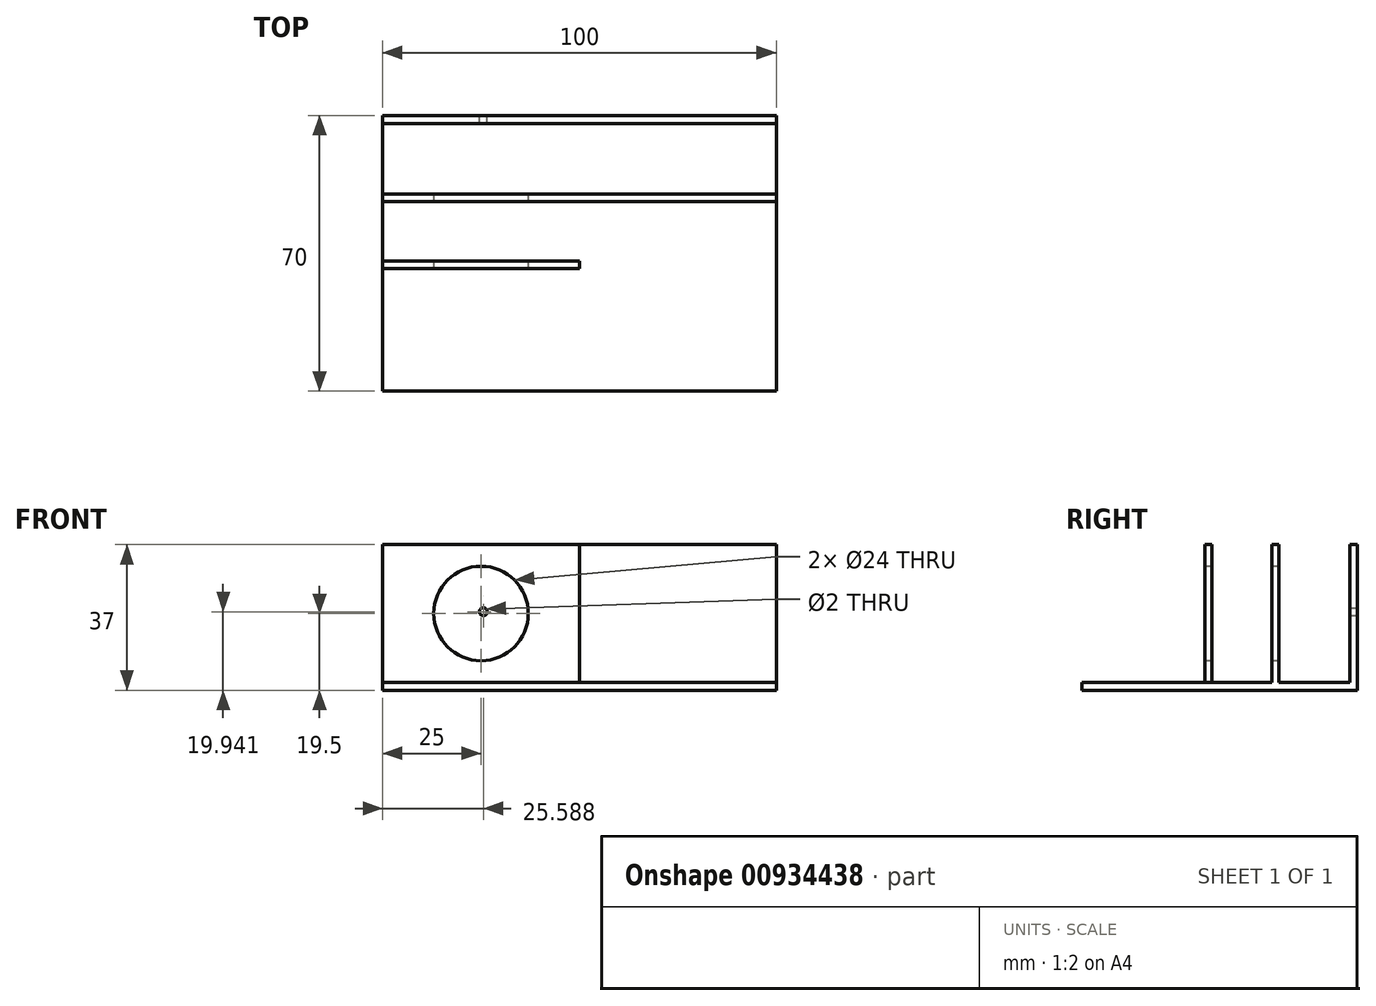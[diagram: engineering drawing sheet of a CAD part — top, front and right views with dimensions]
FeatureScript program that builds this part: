
annotation { "Feature Type Name" : "Feature", "Feature Type Description" : "" }
export const myFeature = defineFeature(function(context is Context, id is Id, definition is map)
    precondition{}
    {
        {
            var Q0;
            Q0=qCreatedBy(makeId("Top.planeOp"),FACE);
            var sketch = newSketch(context, id + "F0", { "sketchPlane" : qUnion([Q0])});
            skLineSegment(sketch, "E0.bottom", {"start": v(-50, 35) * mm, "end": v(50, 35) * mm});
            skLineSegment(sketch, "E0.top", {"start": v(-50, -35) * mm, "end": v(50, -35) * mm});
            skLineSegment(sketch, "E0.left", {"start": v(-50, 35) * mm, "end": v(-50, -35) * mm});
            skLineSegment(sketch, "E0.right", {"start": v(50, 35) * mm, "end": v(50, -35) * mm});
            skPoint(sketch, "E0.middle", {"position": v(0, 0) * mm});
            skSolve(sketch);
        }
        {
            var Q0;
            Q0=makeQuery(id+"F0.imprint","IMPRINT",FACE,{"disambiguationData":[TD([[makeQuery(id+"F0.imprint","IMPRINT",EDGE,{"derivedFrom":sQuery(id+"F0.wireOp",EDGE,"E0.bottom")}),-1.0]])]});
            extrude(context, id + "F1", {"entities" : qUnion([Q0]), "oppositeDirection" : true, "depth" : 2 * mm, "offsetDistance" : 25 * mm});
        }
        {
            var Q0;
            Q0=makeQuery(id+"F1.opExtrude","CAP_FACE",FACE,{"disambiguationData":[OSD([sQuery(id+"F0.wireOp",EDGE,"E0.bottom"),sQuery(id+"F0.wireOp",EDGE,"E0.top"),sQuery(id+"F0.wireOp",EDGE,"E0.left"),sQuery(id+"F0.wireOp",EDGE,"E0.right")])],"isStart":true});
            var sketch = newSketch(context, id + "F2", { "sketchPlane" : qUnion([Q0])});
            skLineSegment(sketch, "E1.bottom", {"start": v(-50, 35) * mm, "end": v(50, 35) * mm});
            skLineSegment(sketch, "E1.top", {"start": v(-50, 33) * mm, "end": v(50, 33) * mm});
            skLineSegment(sketch, "E1.left", {"start": v(-50, 35) * mm, "end": v(-50, 33) * mm});
            skLineSegment(sketch, "E1.right", {"start": v(50, 35) * mm, "end": v(50, 33) * mm});
            skLineSegment(sketch, "E2.bottom", {"start": v(-50, 15) * mm, "end": v(50, 15) * mm});
            skLineSegment(sketch, "E2.top", {"start": v(-50, 13.2) * mm, "end": v(50, 13.2) * mm});
            skLineSegment(sketch, "E2.left", {"start": v(-50, 15) * mm, "end": v(-50, 13.2) * mm});
            skLineSegment(sketch, "E2.right", {"start": v(50, 15) * mm, "end": v(50, 13.2) * mm});
            skLineSegment(sketch, "E3.bottom", {"start": v(-50, -2) * mm, "end": v(50, -2) * mm});
            skLineSegment(sketch, "E3.top", {"start": v(-50, -3.8) * mm, "end": v(50, -3.8) * mm});
            skLineSegment(sketch, "E3.left", {"start": v(-50, -2) * mm, "end": v(-50, -3.8) * mm});
            skLineSegment(sketch, "E3.right", {"start": v(50, -2) * mm, "end": v(50, -3.8) * mm});
            skLineSegment(sketch, "E4", {"start": v(0, -3.8) * mm, "end": v(0, -2) * mm});
            skLineSegment(sketch, "E5", {"start": v(0, 13.2) * mm, "end": v(0, 15) * mm});
            skSolve(sketch);
        }
        {
            var Q0;
            Q0=makeQuery(id+"F2.imprint","IMPRINT",FACE,{"disambiguationData":[TD([[makeQuery(id+"F2.imprint","IMPRINT",EDGE,{"derivedFrom":sQuery(id+"F2.wireOp",EDGE,"E1.bottom")}),-1.0]])]});
            var Q1;
            {var subQ0=sQuery(id+"F2.wireOp",EDGE,"E2.left");Q1=makeQuery(id+"F2.imprint","IMPRINT",FACE,{"disambiguationData":[TD([[makeQuery(id+"F2.imprint","IMPRINT",EDGE,{"derivedFrom":subQ0}),1.0]])]});}
            var Q2;
            {var subQ0=sQuery(id+"F2.wireOp",EDGE,"E3.left");Q2=makeQuery(id+"F2.imprint","IMPRINT",FACE,{"disambiguationData":[TD([[makeQuery(id+"F2.imprint","IMPRINT",EDGE,{"derivedFrom":subQ0}),1.0]])]});}
            var Q3;
            {var subQ0=sQuery(id+"F2.wireOp",EDGE,"E2.right");Q3=makeQuery(id+"F2.imprint","IMPRINT",FACE,{"disambiguationData":[TD([[makeQuery(id+"F2.imprint","IMPRINT",EDGE,{"derivedFrom":subQ0}),-1.0]])]});}
            extrude(context, id + "F3", {"entities" : qUnion([Q0, Q1, Q2, Q3]), "operationType" : NewBodyOperationType.ADD, "depth" : 35 * mm, "offsetDistance" : 25 * mm});
        }
        {
            var Q0;
            Q0=makeQuery(id+"F3.opExtrude","SWEPT_FACE",FACE,{"disambiguationData":[OSD([sQuery(id+"F2.wireOp",EDGE,"E3.top")])]});
            var sketch = newSketch(context, id + "F4", { "sketchPlane" : qUnion([Q0])});
            skLineSegment(sketch, "E6", {"start": v(-50, 0) * mm, "end": v(0, 0) * mm, "construction": true});
            skLineSegment(sketch, "E7", {"start": v(0, 0) * mm, "end": v(0, 35) * mm, "construction": true});
            skLineSegment(sketch, "E8", {"start": v(-25, 0) * mm, "end": v(-25, 35) * mm, "construction": true});
            skLineSegment(sketch, "E9", {"start": v(0, 17.5) * mm, "end": v(-25, 17.5) * mm, "construction": true});
            skLineSegment(sketch, "E10", {"start": v(-25, 17.5) * mm, "end": v(-50, 17.5) * mm, "construction": true});
            skLineSegment(sketch, "E11", {"start": v(-37.5, 17.5) * mm, "end": v(-37.5, 0) * mm, "construction": true});
            skLineSegment(sketch, "E12", {"start": v(-37.5, 17.5) * mm, "end": v(-37.5, 35) * mm, "construction": true});
            skCircle(sketch, "E13", {"center": v(-25, 17.5) * mm, "radius": 12 * mm});
            skSolve(sketch);
        }
        {
            var Q0;
            Q0=makeQuery(id+"F4.imprint","IMPRINT",FACE,{"disambiguationData":[TD([[makeQuery(id+"F4.imprint","IMPRINT",EDGE,{"derivedFrom":sQuery(id+"F4.wireOp",EDGE,"E13")}),1.0]])]});
            extrude(context, id + "F5", {"entities" : qUnion([Q0]), "operationType" : NewBodyOperationType.REMOVE, "oppositeDirection" : true, "depth" : 25 * mm, "offsetDistance" : 25 * mm});
        }
        {
            var Q0;
            Q0=makeQuery(id+"F3.boolean.opBoolean","MERGE",FACE,{"derivedFrom":[makeQuery(id+"F1.opExtrude","SWEPT_FACE",FACE,{"disambiguationData":[OSD([sQuery(id+"F0.wireOp",EDGE,"E0.bottom")])]}),makeQuery(id+"F3.opExtrude","SWEPT_FACE",FACE,{"disambiguationData":[OSD([sQuery(id+"F2.wireOp",EDGE,"E1.bottom")])]})]});
            var sketch = newSketch(context, id + "F6", { "sketchPlane" : qUnion([Q0])});
            skLineSegment(sketch, "E14", {"start": v(-1.18, 17.94) * mm, "end": v(50, 17.94) * mm, "construction": true});
            skLineSegment(sketch, "E15", {"start": v(24.41, 17.94) * mm, "end": v(24.41, 35) * mm, "construction": true});
            skCircle(sketch, "E16", {"center": v(24.41, 17.94) * mm, "radius": 1 * mm});
            skSolve(sketch);
        }
        {
            var Q0;
            Q0=makeQuery(id+"F6.imprint","IMPRINT",FACE,{"disambiguationData":[TD([[makeQuery(id+"F6.imprint","IMPRINT",EDGE,{"derivedFrom":sQuery(id+"F6.wireOp",EDGE,"E16")}),1.0]])]});
            extrude(context, id + "F7", {"entities" : qUnion([Q0]), "operationType" : NewBodyOperationType.REMOVE, "oppositeDirection" : true, "depth" : 5.1 * mm, "offsetDistance" : 25 * mm});
        }
    });
